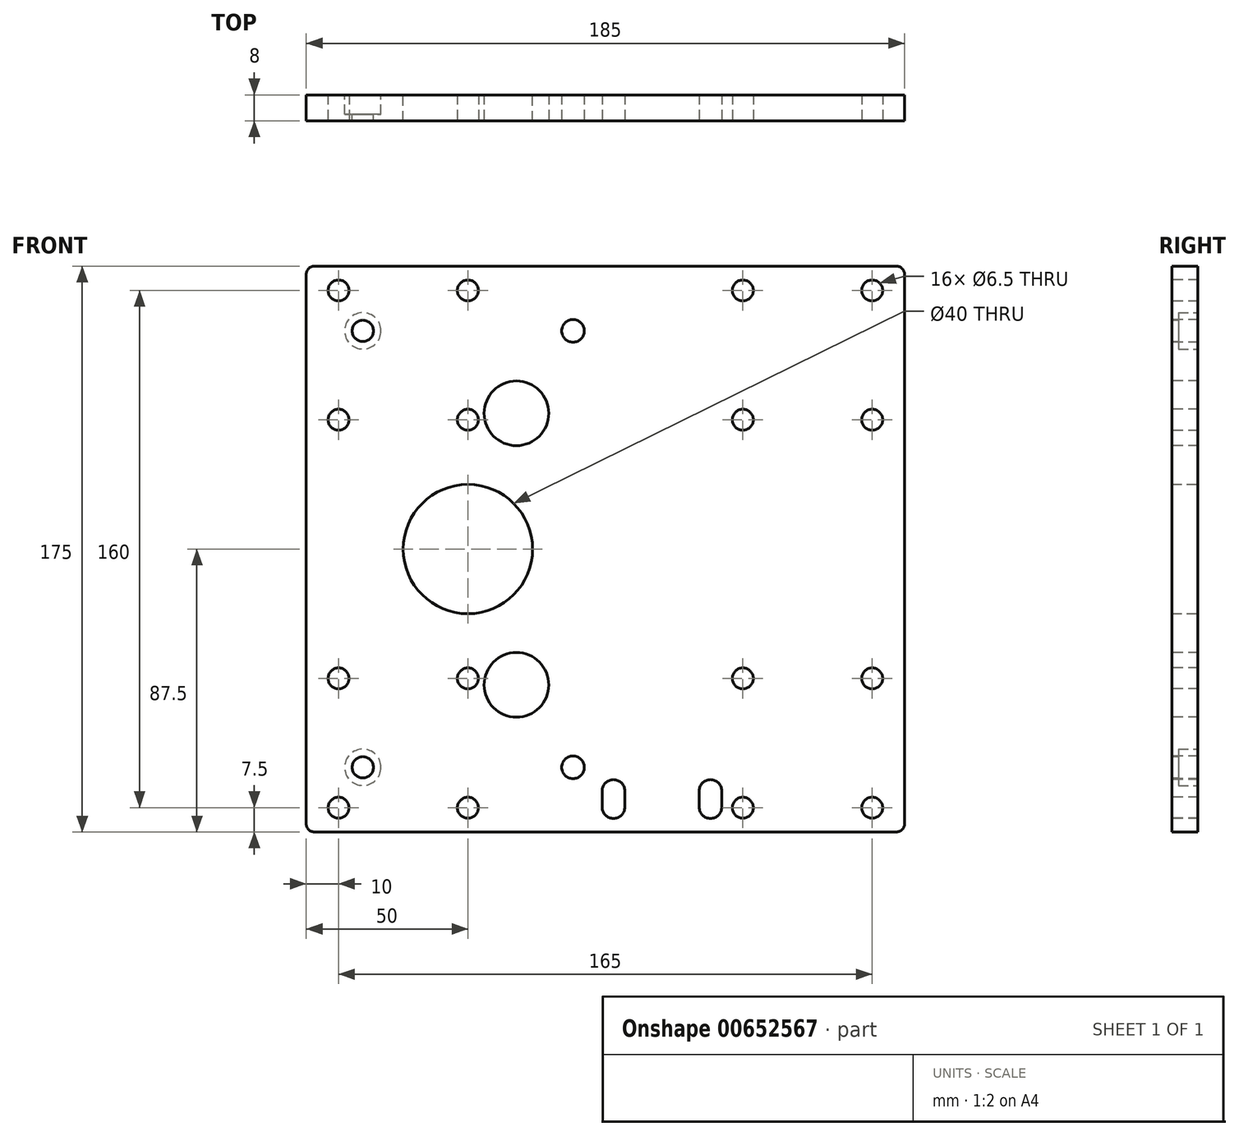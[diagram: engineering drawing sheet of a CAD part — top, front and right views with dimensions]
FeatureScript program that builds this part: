
annotation { "Feature Type Name" : "Feature", "Feature Type Description" : "" }
export const myFeature = defineFeature(function(context is Context, id is Id, definition is map)
    precondition{}
    {
        {
            var Q0;
            Q0=qCreatedBy(makeId("Front.planeOp"),FACE);
            var sketch = newSketch(context, id + "F0", { "sketchPlane" : qUnion([Q0])});
            skLineSegment(sketch, "E0.bottom", {"start": v(92.5, 87.5) * mm, "end": v(-92.5, 87.5) * mm});
            skLineSegment(sketch, "E0.top", {"start": v(92.5, -87.5) * mm, "end": v(-92.5, -87.5) * mm});
            skLineSegment(sketch, "E0.left", {"start": v(92.5, 87.5) * mm, "end": v(92.5, -87.5) * mm});
            skLineSegment(sketch, "E0.right", {"start": v(-92.5, 87.5) * mm, "end": v(-92.5, -87.5) * mm});
            skPoint(sketch, "E0.middle", {"position": v(0, 0) * mm});
            skCircle(sketch, "E1", {"center": v(-42.5, 0) * mm, "radius": 20 * mm});
            skSolve(sketch);
        }
        {
            var Q0;
            Q0 = qSketchRegion(id + "F0", true);
            extrude(context, id + "F1", {"entities" : qUnion([Q0]), "depth" : 8 * mm, "offsetDistance" : 25 * mm});
        }
        {
            var Q0;
            Q0=makeQuery(id+"F1.opExtrude","CAP_FACE",FACE,{"disambiguationData":[OSD([sQuery(id+"F0.wireOp",EDGE,"E0.bottom"),sQuery(id+"F0.wireOp",EDGE,"E0.top"),sQuery(id+"F0.wireOp",EDGE,"E0.left"),sQuery(id+"F0.wireOp",EDGE,"E0.right"),sQuery(id+"F0.wireOp",EDGE,"E1")])],"isStart":false});
            var sketch = newSketch(context, id + "F2", { "sketchPlane" : qUnion([Q0])});
            skPoint(sketch, "E2", {"position": v(-82.5, -40) * mm});
            skPoint(sketch, "E3", {"position": v(-42.5, -40) * mm});
            skPoint(sketch, "E4", {"position": v(-42.5, -80) * mm});
            skPoint(sketch, "E5", {"position": v(-82.5, -80) * mm});
            skPoint(sketch, "E6", {"position": v(42.5, -40) * mm});
            skPoint(sketch, "E7", {"position": v(82.5, -40) * mm});
            skPoint(sketch, "E8", {"position": v(82.5, -80) * mm});
            skPoint(sketch, "E9", {"position": v(42.5, -80) * mm});
            skPoint(sketch, "E10", {"position": v(82.5, 80) * mm});
            skPoint(sketch, "E11", {"position": v(82.5, 40) * mm});
            skPoint(sketch, "E12", {"position": v(42.5, 40) * mm});
            skPoint(sketch, "E13", {"position": v(42.5, 80) * mm});
            skPoint(sketch, "E14", {"position": v(-42.5, 80) * mm});
            skPoint(sketch, "E15", {"position": v(-82.5, 80) * mm});
            skPoint(sketch, "E16", {"position": v(-82.5, 40) * mm});
            skPoint(sketch, "E17", {"position": v(-42.5, 40) * mm});
            skPoint(sketch, "E18", {"position": v(-10, 67.5) * mm});
            skPoint(sketch, "E19", {"position": v(-10, -67.5) * mm});
            skPoint(sketch, "E20", {"position": v(-27.5, 42) * mm});
            skPoint(sketch, "E21", {"position": v(-27.5, -42) * mm});
            skSolve(sketch);
        }
        {
            var Q0;
            Q0=sQuery(id+"F2.wireOp",VERTEX,"E15");
            var Q1;
            Q1=sQuery(id+"F2.wireOp",VERTEX,"E14");
            var Q2;
            Q2=sQuery(id+"F2.wireOp",VERTEX,"E17");
            var Q3;
            Q3=sQuery(id+"F2.wireOp",VERTEX,"E16");
            var Q4;
            Q4=sQuery(id+"F2.wireOp",VERTEX,"E2");
            var Q5;
            Q5=sQuery(id+"F2.wireOp",VERTEX,"E3");
            var Q6;
            Q6=sQuery(id+"F2.wireOp",VERTEX,"E4");
            var Q7;
            Q7=sQuery(id+"F2.wireOp",VERTEX,"E5");
            var Q8;
            Q8=sQuery(id+"F2.wireOp",VERTEX,"E9");
            var Q9;
            Q9=sQuery(id+"F2.wireOp",VERTEX,"E8");
            var Q10;
            Q10=sQuery(id+"F2.wireOp",VERTEX,"E7");
            var Q11;
            Q11=sQuery(id+"F2.wireOp",VERTEX,"E6");
            var Q12;
            Q12=sQuery(id+"F2.wireOp",VERTEX,"E12");
            var Q13;
            Q13=sQuery(id+"F2.wireOp",VERTEX,"E11");
            var Q14;
            Q14=sQuery(id+"F2.wireOp",VERTEX,"E10");
            var Q15;
            Q15=sQuery(id+"F2.wireOp",VERTEX,"E13");
            var Q16;
            Q16=makeQuery(id+"F1.opExtrude","SWEPT_BODY",BODY,{"disambiguationData":[OSD([sQuery(id+"F0.wireOp",EDGE,"E0.bottom"),sQuery(id+"F0.wireOp",EDGE,"E0.top"),sQuery(id+"F0.wireOp",EDGE,"E0.left"),sQuery(id+"F0.wireOp",EDGE,"E0.right"),sQuery(id+"F0.wireOp",EDGE,"E1")])]});
            hole(context, id + "F3", {"style" : HoleStyle.SIMPLE, "endStyle" : HoleEndStyle.THROUGH, "holeDiameter" : 6.5 * mm, "majorDiameter" : 5 * mm, "isTappedThrough" : true, "tappedDepth" : 12 * mm, "tapClearance" : 3, "locations" : qUnion([Q0, Q1, Q2, Q3, Q4, Q5, Q6, Q7, Q8, Q9, Q10, Q11, Q12, Q13, Q14, Q15]), "scope" : qUnion([Q16])});
        }
        {
            var Q0;
            Q0=sQuery(id+"F2.wireOp",VERTEX,"E21");
            var Q1;
            Q1=sQuery(id+"F2.wireOp",VERTEX,"E20");
            var Q2;
            Q2=makeQuery(id+"F1.opExtrude","SWEPT_BODY",BODY,{"disambiguationData":[OSD([sQuery(id+"F0.wireOp",EDGE,"E0.bottom"),sQuery(id+"F0.wireOp",EDGE,"E0.top"),sQuery(id+"F0.wireOp",EDGE,"E0.left"),sQuery(id+"F0.wireOp",EDGE,"E0.right"),sQuery(id+"F0.wireOp",EDGE,"E1")])]});
            hole(context, id + "F4", {"style" : HoleStyle.SIMPLE, "endStyle" : HoleEndStyle.THROUGH, "holeDiameter" : 20 * mm, "majorDiameter" : 5 * mm, "isTappedThrough" : true, "tappedDepth" : 12 * mm, "tapClearance" : 3, "locations" : qUnion([Q0, Q1]), "scope" : qUnion([Q2])});
        }
        {
            var Q0;
            Q0=sQuery(id+"F2.wireOp",VERTEX,"E18");
            var Q1;
            Q1=sQuery(id+"F2.wireOp",VERTEX,"E19");
            var Q2;
            Q2=makeQuery(id+"F1.opExtrude","SWEPT_BODY",BODY,{"disambiguationData":[OSD([sQuery(id+"F0.wireOp",EDGE,"E0.bottom"),sQuery(id+"F0.wireOp",EDGE,"E0.top"),sQuery(id+"F0.wireOp",EDGE,"E0.left"),sQuery(id+"F0.wireOp",EDGE,"E0.right"),sQuery(id+"F0.wireOp",EDGE,"E1")])]});
            hole(context, id + "F5", {"style" : HoleStyle.SIMPLE, "endStyle" : HoleEndStyle.THROUGH, "holeDiameter" : 7 * mm, "majorDiameter" : 5 * mm, "isTappedThrough" : true, "tappedDepth" : 12 * mm, "tapClearance" : 3, "locations" : qUnion([Q0, Q1]), "scope" : qUnion([Q2])});
        }
        {
            var Q0;
            Q0=makeQuery(id+"F2.imprint","IMPRINT",FACE,{"disambiguationData":[TD([[makeQuery(id+"F2.imprint","IMPRINT",EDGE,{"derivedFrom":makeQuery(id+"F1.opExtrude","CAP_EDGE",EDGE,{"disambiguationData":[OSD([sQuery(id+"F0.wireOp",EDGE,"E0.bottom")])],"isStart":false})}),1.0]])]});
            var sketch = newSketch(context, id + "F6", { "sketchPlane" : qUnion([Q0])});
            skArc(sketch, "E22", {"start": v(6, -74.81) * mm, "mid": v(2.5, -71.31) * mm, "end": v(-1, -74.81) * mm});
            skArc(sketch, "E23", {"start": v(-1, -79.81) * mm, "mid": v(2.5, -83.31) * mm, "end": v(6, -79.81) * mm});
            skLineSegment(sketch, "E24", {"start": v(-1, -74.81) * mm, "end": v(-1, -79.81) * mm});
            skLineSegment(sketch, "E25", {"start": v(6, -74.81) * mm, "end": v(6, -79.81) * mm});
            skArc(sketch, "E26", {"start": v(36, -74.81) * mm, "mid": v(32.5, -71.31) * mm, "end": v(29, -74.81) * mm});
            skArc(sketch, "E27", {"start": v(29, -79.81) * mm, "mid": v(32.5, -83.31) * mm, "end": v(36, -79.81) * mm});
            skLineSegment(sketch, "E28", {"start": v(29, -74.81) * mm, "end": v(29, -79.81) * mm});
            skLineSegment(sketch, "E29", {"start": v(36, -74.81) * mm, "end": v(36, -79.81) * mm});
            skSolve(sketch);
        }
        {
            var Q0;
            Q0 = qSketchRegion(id + "F6", true);
            extrude(context, id + "F7", {"entities" : qUnion([Q0]), "operationType" : NewBodyOperationType.REMOVE, "oppositeDirection" : true, "depth" : 25 * mm, "offsetDistance" : 25 * mm});
        }
        {
            var Q0;
            Q0=makeQuery(id+"F1.opExtrude","CAP_FACE",FACE,{"disambiguationData":[OSD([sQuery(id+"F0.wireOp",EDGE,"E0.bottom"),sQuery(id+"F0.wireOp",EDGE,"E0.top"),sQuery(id+"F0.wireOp",EDGE,"E0.left"),sQuery(id+"F0.wireOp",EDGE,"E0.right"),sQuery(id+"F0.wireOp",EDGE,"E1")])],"isStart":true});
            var sketch = newSketch(context, id + "F8", { "sketchPlane" : qUnion([Q0])});
            skPoint(sketch, "E30", {"position": v(75, 67.5) * mm});
            skPoint(sketch, "E31", {"position": v(75, -67.5) * mm});
            skSolve(sketch);
        }
        {
            var Q0;
            Q0=sQuery(id+"F8.wireOp",VERTEX,"E30");
            var Q1;
            Q1=sQuery(id+"F8.wireOp",VERTEX,"E31");
            var Q2;
            Q2=makeQuery(id+"F1.opExtrude","SWEPT_BODY",BODY,{"disambiguationData":[OSD([sQuery(id+"F0.wireOp",EDGE,"E0.bottom"),sQuery(id+"F0.wireOp",EDGE,"E0.top"),sQuery(id+"F0.wireOp",EDGE,"E0.left"),sQuery(id+"F0.wireOp",EDGE,"E0.right"),sQuery(id+"F0.wireOp",EDGE,"E1")])]});
            hole(context, id + "F9", {"style" : HoleStyle.C_BORE, "endStyle" : HoleEndStyle.THROUGH, "standardTappedOrClearance" : lookupTablePath({ "standard" : "ISO", "fit" : "Normal", "size" : "M6", "type" : "Clearance" }), "standardBlindInLast" : lookupTablePath({ "fit" : "Standard", "standard" : "ISO", "size" : "M6", "type" : "Clearance" }), "holeDiameter" : 6.6 * mm, "cBoreDiameter" : 11.25 * mm, "cBoreDepth" : 6 * mm, "majorDiameter" : 5 * mm, "isTappedThrough" : true, "tappedDepth" : 12 * mm, "tapClearance" : 3, "locations" : qUnion([Q0, Q1]), "scope" : qUnion([Q2])});
        }
        {
            var Q0;
            Q0=makeQuery(id+"F1.opExtrude","SWEPT_EDGE",EDGE,{"disambiguationData":[OSD([sQuery(id+"F0.wireOp",EDGE,"E0.bottom"),sQuery(id+"F0.wireOp",EDGE,"E0.right")])]});
            var Q1;
            Q1=makeQuery(id+"F1.opExtrude","SWEPT_EDGE",EDGE,{"disambiguationData":[OSD([sQuery(id+"F0.wireOp",EDGE,"E0.top"),sQuery(id+"F0.wireOp",EDGE,"E0.right")])]});
            var Q2;
            Q2=makeQuery(id+"F1.opExtrude","SWEPT_EDGE",EDGE,{"disambiguationData":[OSD([sQuery(id+"F0.wireOp",EDGE,"E0.top"),sQuery(id+"F0.wireOp",EDGE,"E0.left")])]});
            var Q3;
            Q3=makeQuery(id+"F1.opExtrude","SWEPT_EDGE",EDGE,{"disambiguationData":[OSD([sQuery(id+"F0.wireOp",EDGE,"E0.bottom"),sQuery(id+"F0.wireOp",EDGE,"E0.left")])]});
            fillet(context, id + "F10", {"entities" : qUnion([Q0, Q1, Q2, Q3]), "radius" : 2.5 * mm, "tangentPropagation" : true, "allowEdgeOverflow" : false});
        }
    });
